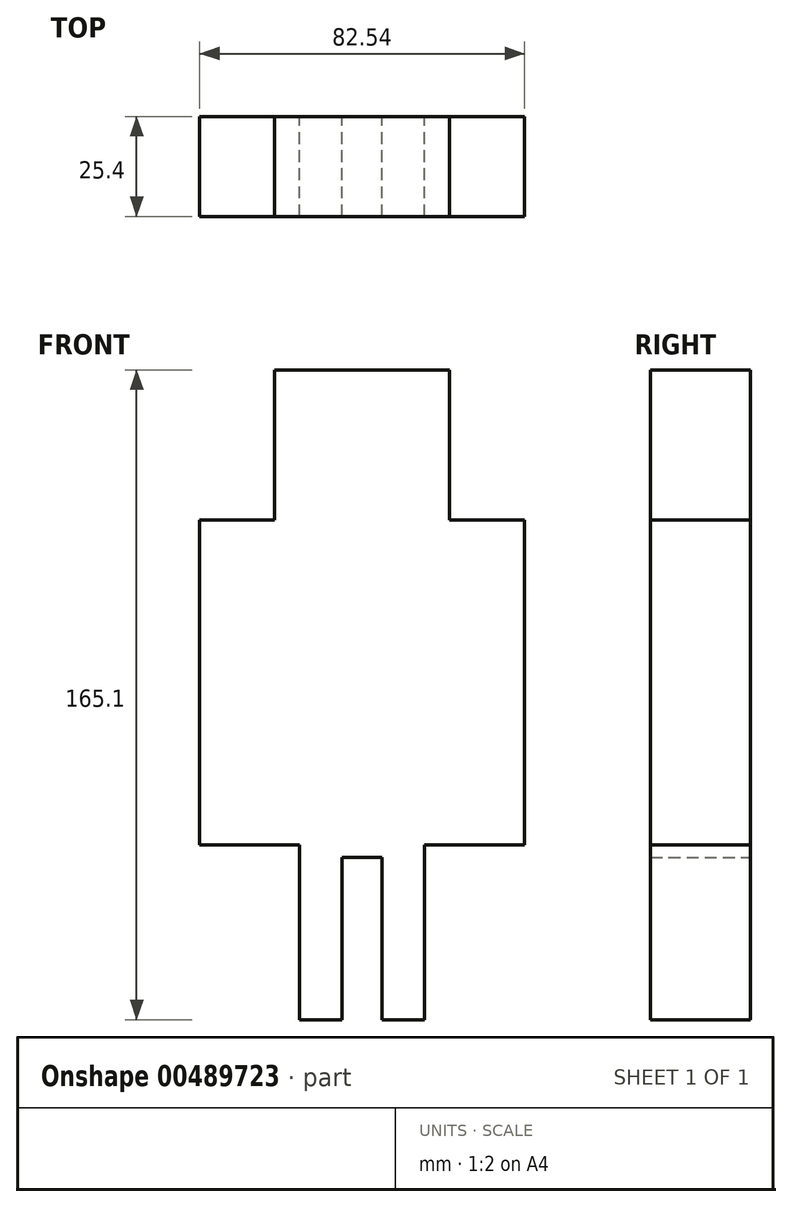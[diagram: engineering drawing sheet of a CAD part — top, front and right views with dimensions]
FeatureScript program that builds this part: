
annotation { "Feature Type Name" : "Feature", "Feature Type Description" : "" }
export const myFeature = defineFeature(function(context is Context, id is Id, definition is map)
    precondition{}
    {
        {
            var Q0;
            Q0=qCreatedBy(makeId("Front.planeOp"),FACE);
            var sketch = newSketch(context, id + "F0", { "sketchPlane" : qUnion([Q0])});
            skLineSegment(sketch, "E0.bottom", {"start": v(22.24, 82.55) * mm, "end": v(-22.23, 82.55) * mm});
            skLineSegment(sketch, "E0.top", {"start": v(15.88, -82.55) * mm, "end": v(5.08, -82.55) * mm});
            skLineSegment(sketch, "E0.left", {"start": v(41.28, 44.45) * mm, "end": v(41.28, -38.1) * mm});
            skLineSegment(sketch, "E0.right", {"start": v(-41.27, 44.45) * mm, "end": v(-41.28, -38.1) * mm});
            skPoint(sketch, "E0.middle", {"position": v(0, 0) * mm});
            skLineSegment(sketch, "E1.top", {"start": v(-41.28, 44.45) * mm, "end": v(-22.23, 44.45) * mm});
            skLineSegment(sketch, "E1.right", {"start": v(-22.23, 82.55) * mm, "end": v(-22.23, 44.45) * mm});
            skLineSegment(sketch, "E2.top", {"start": v(41.28, 44.45) * mm, "end": v(22.24, 44.45) * mm});
            skLineSegment(sketch, "E2.right", {"start": v(22.24, 82.55) * mm, "end": v(22.24, 44.45) * mm});
            skPoint(sketch, "E3.orphan", {"position": v(41.28, 82.55) * mm});
            skPoint(sketch, "E4.orphan", {"position": v(-41.27, 82.55) * mm});
            skLineSegment(sketch, "E5.top", {"start": v(-41.28, -38.1) * mm, "end": v(-15.88, -38.1) * mm});
            skLineSegment(sketch, "E5.right", {"start": v(-15.88, -82.55) * mm, "end": v(-15.88, -38.1) * mm});
            skLineSegment(sketch, "E6.top", {"start": v(41.28, -38.1) * mm, "end": v(15.88, -38.1) * mm});
            skLineSegment(sketch, "E6.right", {"start": v(15.88, -82.55) * mm, "end": v(15.88, -38.1) * mm});
            skPoint(sketch, "E7.orphan", {"position": v(-41.28, -82.55) * mm});
            skPoint(sketch, "E8.orphan", {"position": v(41.27, -82.55) * mm});
            skLineSegment(sketch, "E9.bottom", {"start": v(-5.08, -41.28) * mm, "end": v(5.08, -41.28) * mm});
            skLineSegment(sketch, "E9.left", {"start": v(-5.08, -41.28) * mm, "end": v(-5.08, -82.55) * mm});
            skLineSegment(sketch, "E9.right", {"start": v(5.08, -41.28) * mm, "end": v(5.08, -82.55) * mm});
            skPoint(sketch, "E9.middle", {"position": v(0, -82.55) * mm});
            skPoint(sketch, "E9.top.end.orphan", {"position": v(5.08, -123.83) * mm});
            skPoint(sketch, "E9.top.start.orphan", {"position": v(-5.08, -123.83) * mm});
            skLineSegment(sketch, "E10.trimOffspring", {"start": v(-5.08, -82.55) * mm, "end": v(-15.88, -82.55) * mm});
            skSolve(sketch);
        }
        {
            var Q0;
            Q0=makeQuery(id+"F0.imprint","IMPRINT",FACE,{"disambiguationData":[TD([[makeQuery(id+"F0.imprint","IMPRINT",EDGE,{"derivedFrom":sQuery(id+"F0.wireOp",EDGE,"E0.bottom")}),1.0]])]});
            extrude(context, id + "F1", {"entities" : qUnion([Q0]), "depth" : 25.4 * mm});
        }
    });
